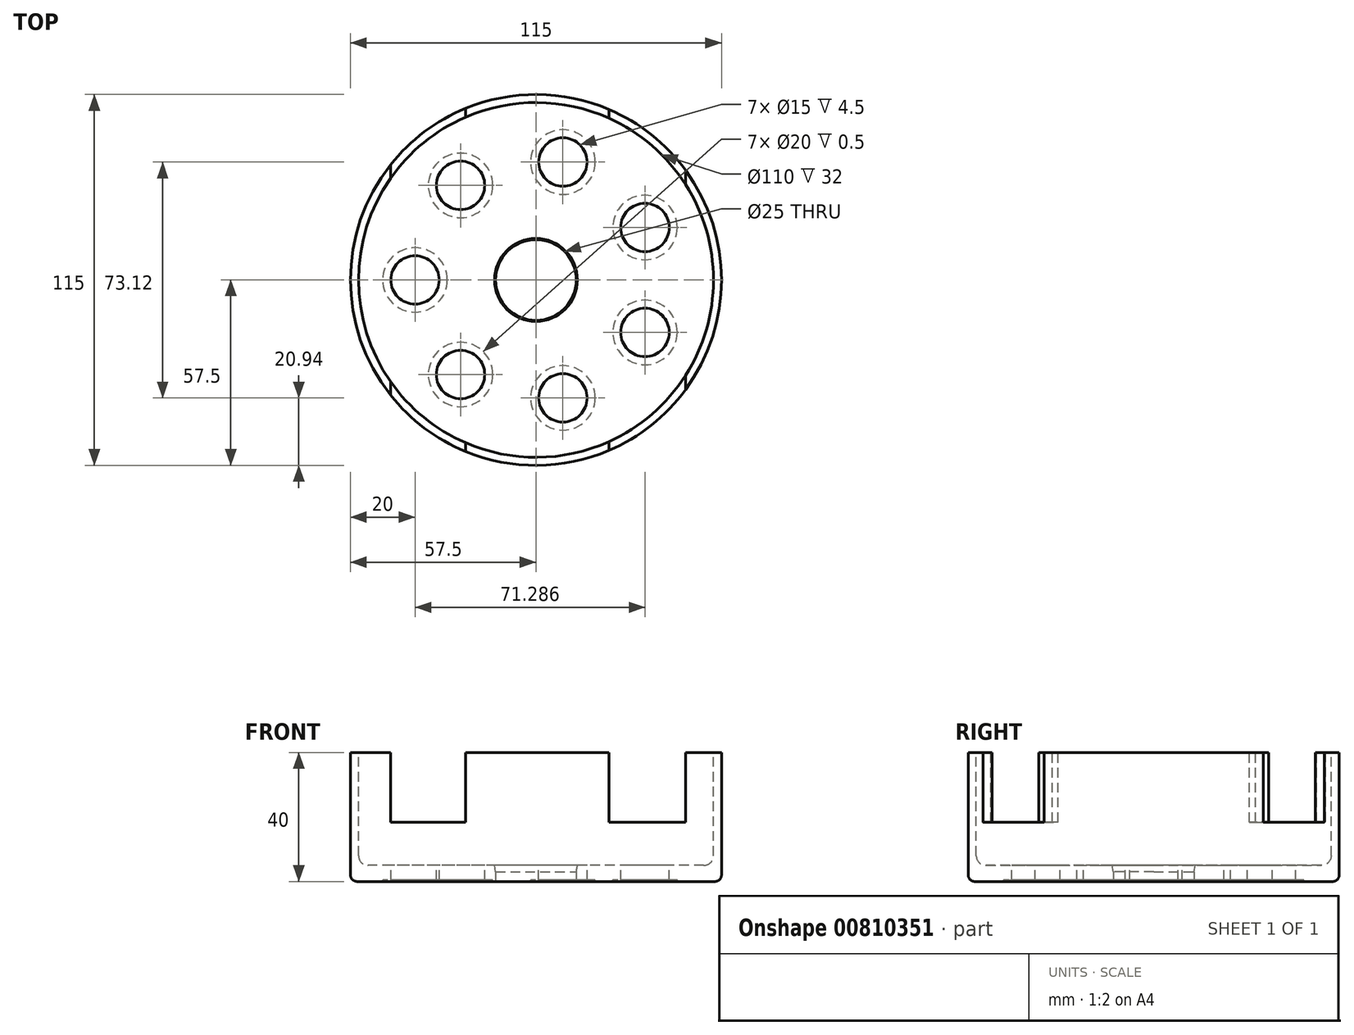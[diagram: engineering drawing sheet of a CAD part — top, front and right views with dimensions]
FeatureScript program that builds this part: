
annotation { "Feature Type Name" : "Feature", "Feature Type Description" : "" }
export const myFeature = defineFeature(function(context is Context, id is Id, definition is map)
    precondition{}
    {
        {
            var Q0;
            Q0=qCreatedBy(makeId("Top.planeOp"),FACE);
            var sketch = newSketch(context, id + "F0", { "sketchPlane" : qUnion([Q0])});
            skCircle(sketch, "E0", {"center": v(0, 0) * mm, "radius": 57.5 * mm});
            skSolve(sketch);
        }
        {
            var Q0;
            Q0 = qSketchRegion(id + "F0", true);
            extrude(context, id + "F1", {"entities" : qUnion([Q0]), "depth" : 40 * mm, "offsetDistance" : 25 * mm});
        }
        {
            var Q0;
            Q0=makeQuery(id+"F1.opExtrude","CAP_FACE",FACE,{"disambiguationData":[OSD([sQuery(id+"F0.wireOp",EDGE,"E0")])],"isStart":false});
            var sketch = newSketch(context, id + "F2", { "sketchPlane" : qUnion([Q0])});
            skCircle(sketch, "E1", {"center": v(0, 0) * mm, "radius": 55 * mm});
            skSolve(sketch);
        }
        {
            var Q0;
            Q0 = qSketchRegion(id + "F2", true);
            extrude(context, id + "F3", {"entities" : qUnion([Q0]), "operationType" : NewBodyOperationType.REMOVE, "oppositeDirection" : true, "depth" : 35 * mm, "offsetDistance" : 25 * mm});
        }
        {
            var Q0;
            Q0=makeQuery(id+"F3.boolean.opBoolean","COPY",EDGE,{"derivedFrom":makeQuery(id+"F3.opExtrude","CAP_EDGE",EDGE,{"disambiguationData":[OSD([sQuery(id+"F2.wireOp",EDGE,"E1")])],"isStart":false})});
            fillet(context, id + "F4", {"entities" : qUnion([Q0]), "radius" : 3 * mm, "tangentPropagation" : true, "allowEdgeOverflow" : false});
        }
        {
            var Q0;
            Q0=makeQuery(id+"F1.opExtrude","CAP_EDGE",EDGE,{"disambiguationData":[OSD([sQuery(id+"F0.wireOp",EDGE,"E0")])],"isStart":true});
            fillet(context, id + "F5", {"entities" : qUnion([Q0]), "radius" : 2 * mm, "tangentPropagation" : true, "allowEdgeOverflow" : false});
        }
        {
            var Q0;
            Q0=makeQuery(id+"F1.opExtrude","CAP_FACE",FACE,{"disambiguationData":[OSD([sQuery(id+"F0.wireOp",EDGE,"E0")])],"isStart":true});
            var sketch = newSketch(context, id + "F6", { "sketchPlane" : qUnion([Q0])});
            skCircle(sketch, "E2", {"center": v(0, 0) * mm, "radius": 12.5 * mm});
            skSolve(sketch);
        }
        {
            var Q0;
            Q0 = qSketchRegion(id + "F6", true);
            extrude(context, id + "F7", {"entities" : qUnion([Q0]), "operationType" : NewBodyOperationType.REMOVE, "endBound" : BoundingType.THROUGH_ALL, "oppositeDirection" : true, "depth" : 25 * mm, "offsetDistance" : 25 * mm});
        }
        {
            var Q0;
            Q0=makeQuery(id+"F1.opExtrude","CAP_FACE",FACE,{"disambiguationData":[OSD([sQuery(id+"F0.wireOp",EDGE,"E0")])],"isStart":true});
            var sketch = newSketch(context, id + "F8", { "sketchPlane" : qUnion([Q0])});
            skCircle(sketch, "E3", {"center": v(0, 0) * mm, "radius": 37.5 * mm});
            skPoint(sketch, "E4", {"position": v(-37.5, 0) * mm});
            skPoint(sketch, "E5.1.0", {"position": v(-23.38, -29.32) * mm});
            skPoint(sketch, "E5.2.0", {"position": v(8.34, -36.56) * mm});
            skPoint(sketch, "E5.3.0", {"position": v(33.79, -16.27) * mm});
            skPoint(sketch, "E5.4.0", {"position": v(33.79, 16.27) * mm});
            skPoint(sketch, "E5.5.0", {"position": v(8.34, 36.56) * mm});
            skPoint(sketch, "E5.6.0", {"position": v(-23.38, 29.32) * mm});
            skSolve(sketch);
        }
        {
            var Q0;
            Q0=sQuery(id+"F8.wireOp",VERTEX,"E4");
            var Q1;
            Q1=sQuery(id+"F8.wireOp",VERTEX,"E5.6.0");
            var Q2;
            Q2=sQuery(id+"F8.wireOp",VERTEX,"E5.5.0");
            var Q3;
            Q3=sQuery(id+"F8.wireOp",VERTEX,"E5.4.0");
            var Q4;
            Q4=sQuery(id+"F8.wireOp",VERTEX,"E5.3.0");
            var Q5;
            Q5=sQuery(id+"F8.wireOp",VERTEX,"E5.2.0");
            var Q6;
            Q6=sQuery(id+"F8.wireOp",VERTEX,"E5.1.0");
            var Q7;
            Q7=makeQuery(id+"F1.opExtrude","SWEPT_BODY",BODY,{"disambiguationData":[OSD([sQuery(id+"F0.wireOp",EDGE,"E0")])]});
            hole(context, id + "F9", {"style" : HoleStyle.C_BORE, "endStyle" : HoleEndStyle.THROUGH, "holeDiameter" : 15 * mm, "cBoreDiameter" : 20 * mm, "cBoreDepth" : 0.5 * mm, "majorDiameter" : 5 * mm, "isTappedThrough" : true, "tappedDepth" : 12 * mm, "tapClearance" : 3, "locations" : qUnion([Q0, Q1, Q2, Q3, Q4, Q5, Q6]), "scope" : qUnion([Q7]), "startStyle" : HoleStartStyle.PART});
        }
        {
            var Q0;
            Q0=makeQuery(id+"F9.hole-4.boolean.opBoolean","INTERSECT",EDGE,{"derivedFrom":[makeQuery(id+"F3.boolean.opBoolean","COPY",FACE,{"derivedFrom":makeQuery(id+"F3.opExtrude","CAP_FACE",FACE,{"disambiguationData":[OSD([sQuery(id+"F2.wireOp",EDGE,"E1")])],"isStart":false})}),makeQuery(id+"F9.hole-4.opRevolve","SWEPT_FACE",FACE,{"disambiguationData":[OSD([sQuery(id+"F9.hole-4.sketch.wireOp",EDGE,"core_line_2")])]})]});
            var Q1;
            Q1=makeQuery(id+"F9.hole-3.boolean.opBoolean","INTERSECT",EDGE,{"derivedFrom":[makeQuery(id+"F3.boolean.opBoolean","COPY",FACE,{"derivedFrom":makeQuery(id+"F3.opExtrude","CAP_FACE",FACE,{"disambiguationData":[OSD([sQuery(id+"F2.wireOp",EDGE,"E1")])],"isStart":false})}),makeQuery(id+"F9.hole-3.opRevolve","SWEPT_FACE",FACE,{"disambiguationData":[OSD([sQuery(id+"F9.hole-3.sketch.wireOp",EDGE,"core_line_2")])]})]});
            var Q2;
            Q2=makeQuery(id+"F9.hole-2.boolean.opBoolean","INTERSECT",EDGE,{"derivedFrom":[makeQuery(id+"F3.boolean.opBoolean","COPY",FACE,{"derivedFrom":makeQuery(id+"F3.opExtrude","CAP_FACE",FACE,{"disambiguationData":[OSD([sQuery(id+"F2.wireOp",EDGE,"E1")])],"isStart":false})}),makeQuery(id+"F9.hole-2.opRevolve","SWEPT_FACE",FACE,{"disambiguationData":[OSD([sQuery(id+"F9.hole-2.sketch.wireOp",EDGE,"core_line_2")])]})]});
            var Q3;
            Q3=makeQuery(id+"F9.hole-1.boolean.opBoolean","INTERSECT",EDGE,{"derivedFrom":[makeQuery(id+"F3.boolean.opBoolean","COPY",FACE,{"derivedFrom":makeQuery(id+"F3.opExtrude","CAP_FACE",FACE,{"disambiguationData":[OSD([sQuery(id+"F2.wireOp",EDGE,"E1")])],"isStart":false})}),makeQuery(id+"F9.hole-1.opRevolve","SWEPT_FACE",FACE,{"disambiguationData":[OSD([sQuery(id+"F9.hole-1.sketch.wireOp",EDGE,"core_line_2")])]})]});
            var Q4;
            Q4=makeQuery(id+"F9.hole-0.boolean.opBoolean","INTERSECT",EDGE,{"derivedFrom":[makeQuery(id+"F3.boolean.opBoolean","COPY",FACE,{"derivedFrom":makeQuery(id+"F3.opExtrude","CAP_FACE",FACE,{"disambiguationData":[OSD([sQuery(id+"F2.wireOp",EDGE,"E1")])],"isStart":false})}),makeQuery(id+"F9.hole-0.opRevolve","SWEPT_FACE",FACE,{"disambiguationData":[OSD([sQuery(id+"F9.hole-0.sketch.wireOp",EDGE,"core_line_2")])]})]});
            var Q5;
            Q5=makeQuery(id+"F9.hole-6.boolean.opBoolean","INTERSECT",EDGE,{"derivedFrom":[makeQuery(id+"F3.boolean.opBoolean","COPY",FACE,{"derivedFrom":makeQuery(id+"F3.opExtrude","CAP_FACE",FACE,{"disambiguationData":[OSD([sQuery(id+"F2.wireOp",EDGE,"E1")])],"isStart":false})}),makeQuery(id+"F9.hole-6.opRevolve","SWEPT_FACE",FACE,{"disambiguationData":[OSD([sQuery(id+"F9.hole-6.sketch.wireOp",EDGE,"core_line_2")])]})]});
            var Q6;
            Q6=makeQuery(id+"F9.hole-5.boolean.opBoolean","INTERSECT",EDGE,{"derivedFrom":[makeQuery(id+"F3.boolean.opBoolean","COPY",FACE,{"derivedFrom":makeQuery(id+"F3.opExtrude","CAP_FACE",FACE,{"disambiguationData":[OSD([sQuery(id+"F2.wireOp",EDGE,"E1")])],"isStart":false})}),makeQuery(id+"F9.hole-5.opRevolve","SWEPT_FACE",FACE,{"disambiguationData":[OSD([sQuery(id+"F9.hole-5.sketch.wireOp",EDGE,"core_line_2")])]})]});
            var Q7;
            Q7=makeQuery(id+"F7.boolean.opBoolean","INTERSECT",EDGE,{"derivedFrom":[makeQuery(id+"F3.boolean.opBoolean","COPY",FACE,{"derivedFrom":makeQuery(id+"F3.opExtrude","CAP_FACE",FACE,{"disambiguationData":[OSD([sQuery(id+"F2.wireOp",EDGE,"E1")])],"isStart":false})}),makeQuery(id+"F7.opExtrude","SWEPT_FACE",FACE,{"disambiguationData":[OSD([sQuery(id+"F6.wireOp",EDGE,"E2")])]})]});
            chamfer(context, id + "F10", {"entities" : qUnion([Q0, Q1, Q2, Q3, Q4, Q5, Q6, Q7]), "chamferType" : ChamferType.OFFSET_ANGLE, "width" : 2 * mm, "oppositeDirection" : false, "angle" : 10 * degree});
        }
        {
            var Q0;
            Q0=qCreatedBy(makeId("Front.planeOp"),FACE);
            var sketch = newSketch(context, id + "F11", { "sketchPlane" : qUnion([Q0])});
            skLineSegment(sketch, "E6.bottom", {"start": v(-45.1, 46.36) * mm, "end": v(-21.86, 46.36) * mm});
            skLineSegment(sketch, "E6.top", {"start": v(-45.1, 18.42) * mm, "end": v(-21.86, 18.42) * mm});
            skLineSegment(sketch, "E6.left", {"start": v(-45.1, 46.36) * mm, "end": v(-45.1, 18.42) * mm});
            skLineSegment(sketch, "E6.right", {"start": v(-21.86, 46.36) * mm, "end": v(-21.86, 18.42) * mm});
            skLineSegment(sketch, "E7.bottom", {"start": v(46.36, 46.54) * mm, "end": v(22.6, 46.54) * mm});
            skLineSegment(sketch, "E7.top", {"start": v(46.36, 18.42) * mm, "end": v(22.6, 18.42) * mm});
            skLineSegment(sketch, "E7.left", {"start": v(46.36, 46.54) * mm, "end": v(46.36, 18.42) * mm});
            skLineSegment(sketch, "E7.right", {"start": v(22.6, 46.54) * mm, "end": v(22.6, 18.42) * mm});
            skSolve(sketch);
        }
        {
            var Q0;
            Q0=makeQuery(id+"F11.imprint","IMPRINT",FACE,{"disambiguationData":[TD([[makeQuery(id+"F11.imprint","IMPRINT",EDGE,{"derivedFrom":sQuery(id+"F11.wireOp",EDGE,"E6.bottom")}),-1.0]])]});
            var Q1;
            Q1=makeQuery(id+"F11.imprint","IMPRINT",FACE,{"disambiguationData":[TD([[makeQuery(id+"F11.imprint","IMPRINT",EDGE,{"derivedFrom":sQuery(id+"F11.wireOp",EDGE,"E7.bottom")}),1.0]])]});
            extrude(context, id + "F12", {"entities" : qUnion([Q0, Q1]), "operationType" : NewBodyOperationType.REMOVE, "endBound" : BoundingType.THROUGH_ALL, "depth" : 25 * mm, "offsetDistance" : 25 * mm, "hasSecondDirection" : true, "secondDirectionBound" : BoundingType.THROUGH_ALL, "secondDirectionOppositeDirection" : true, "secondDirectionDepth" : 25 * mm});
        }
    });
